# Revit family: Flopro Z3 Cuadrado
name_source: partatom
category: Luminarias
revit_build: Autodesk Revit 2015 (Build: 20140606_1530(x64)
units: mm (PartAtom-declared; Revit-internal decimal feet)

## types (6) — shared parameters
Anchura rectángulo de emisión = 207 mm
Cambio de temperatura de color de luz atenuada = <Ninguno>
Fabricante = SECOM ILUMINACIÓN
Filtro de color = 16777215
Forma visible en renderización = No
Longitud de rectángulo de emisión = 207 mm
Lámpara = LED Osram Duris
Ángulo de inclinación = 90.00°

## per-type parameters (varying)
| type | Archivo de red fotométrica | Comentarios de vataje | Descripción | Óptica angulo de apertura |
| Flopro Z3 Cuadrado 18W / 48º | 6160 00 18 84 FLOPRO Z3 LED CUADRADO L48º 18W.IES | 18W | 6160 00 18 84 | 48.00° |
| Flopro Z3 Cuadrado 30W / 11º | 6160 00 30 84 11 FLOPRO Z3 LED CUADRADO L11º 30W.IES | 30W | 6160 00 30 84 11 | 11.00° |
| Flopro Z3 Asimétrico Cuadrado 20W / 48º | 6170 00 20 84 FLOPRO Z3 LED CUADRADO ASIMETRICO L48º 20W.IES | 20W | 6170 00 20 84 | 48.00° |
| Flopro Z3 Cuadrado 18W / 11º | 6160 00 18 84 11 FLOPRO Z3 LED CUADRADO L11º 18W.IES | 18W | 6160 00 18 8411 | 11.00° |
| Flopro Z3 Cuadrado 30W / 48º | 6160 00 30 84 FLOPRO Z3 LED CUADRADO L48º 30W.IES | 30W | 6160 00 30 84 | 48.00° |
| Flopro Z3 Asimétrico Cuadrado 20W / 11º | 6170 00 20 84 11 FLOPRO Z3 LED CUADRADO ASIMETRICO L11º 20W.IES | 20W | 6170 00 20 84 | 11.00° |
